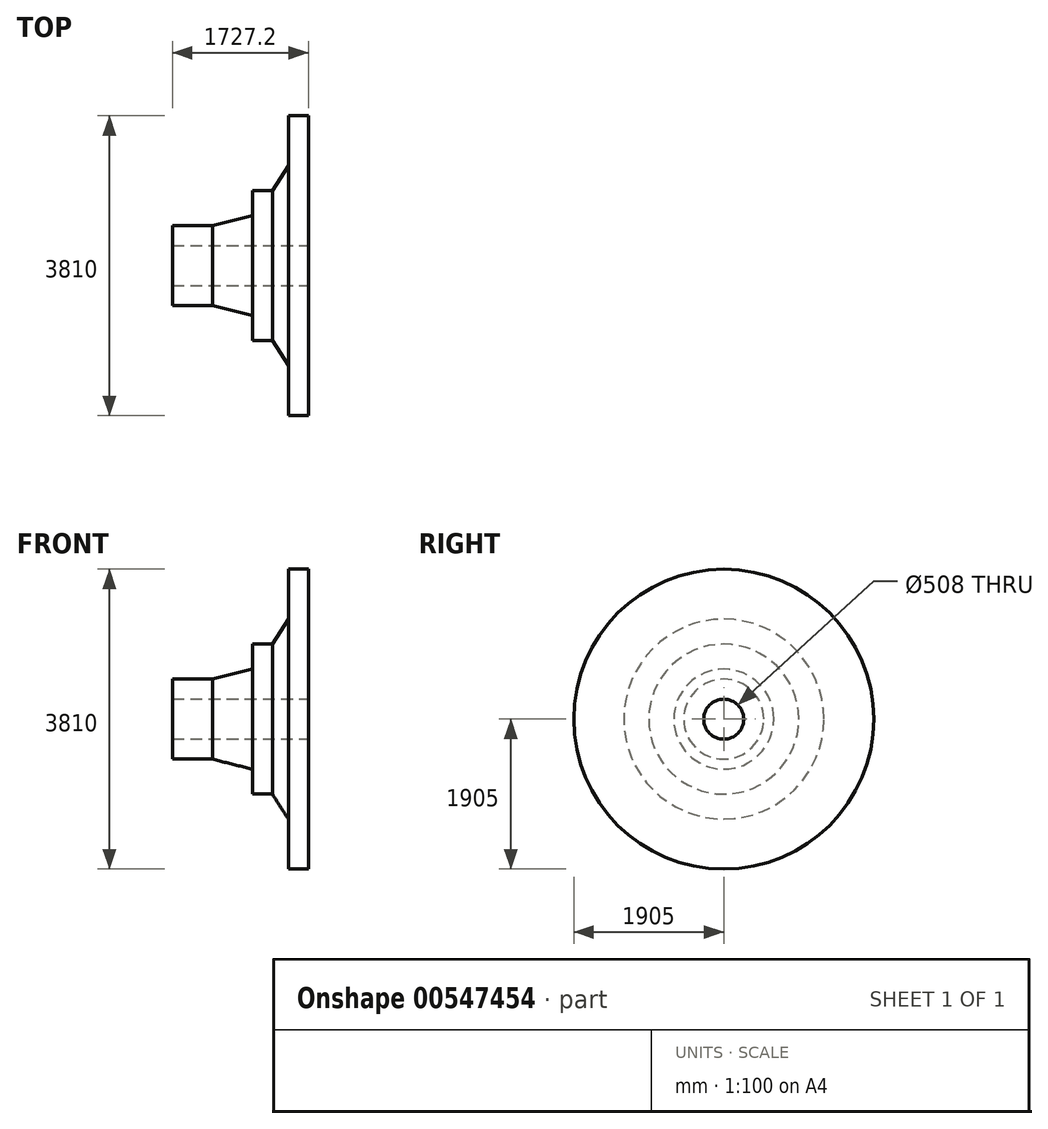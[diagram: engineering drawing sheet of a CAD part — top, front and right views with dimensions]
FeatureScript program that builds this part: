
annotation { "Feature Type Name" : "Feature", "Feature Type Description" : "" }
export const myFeature = defineFeature(function(context is Context, id is Id, definition is map)
    precondition{}
    {
        {
            var Q0;
            Q0=qCreatedBy(makeId("Front.planeOp"),FACE);
            var sketch = newSketch(context, id + "F0", { "sketchPlane" : qUnion([Q0])});
            skLineSegment(sketch, "E0", {"start": v(0, 0) * mm, "end": v(-2711.62, 0) * mm});
            skLineSegment(sketch, "E1", {"start": v(0, 315.78) * mm, "end": v(0, 1905) * mm});
            skLineSegment(sketch, "E2", {"start": v(0, 1905) * mm, "end": v(-254, 1905) * mm});
            skLineSegment(sketch, "E3", {"start": v(-254, 1905) * mm, "end": v(-254, 1270) * mm});
            skLineSegment(sketch, "E4", {"start": v(-254, 1270) * mm, "end": v(-457.2, 952.5) * mm});
            skLineSegment(sketch, "E5", {"start": v(-457.2, 952.5) * mm, "end": v(-711.2, 952.5) * mm});
            skLineSegment(sketch, "E6", {"start": v(-711.2, 952.5) * mm, "end": v(-711.2, 635) * mm});
            skLineSegment(sketch, "E7", {"start": v(-711.2, 635) * mm, "end": v(-1219.2, 508) * mm});
            skLineSegment(sketch, "E8", {"start": v(-1219.2, 508) * mm, "end": v(-1727.2, 508) * mm});
            skLineSegment(sketch, "E9", {"start": v(-1727.2, 508) * mm, "end": v(-1727.2, 254) * mm});
            skLineSegment(sketch, "E10", {"start": v(-1727.2, 254) * mm, "end": v(0, 254) * mm});
            skLineSegment(sketch, "E11", {"start": v(0, 254) * mm, "end": v(0, 1905) * mm});
            skSolve(sketch);
        }
        {
            var Q0;
            Q0=qSketchRegion(id+"F0",true);
            var Q1;
            Q1=sQuery(id+"F0.wireOp",EDGE,"E0");
            revolve(context, id + "F1", {"entities" : qUnion([Q0]), "axis" : qUnion([Q1]), "revolveType" : RevolveType.FULL});
        }
    });
